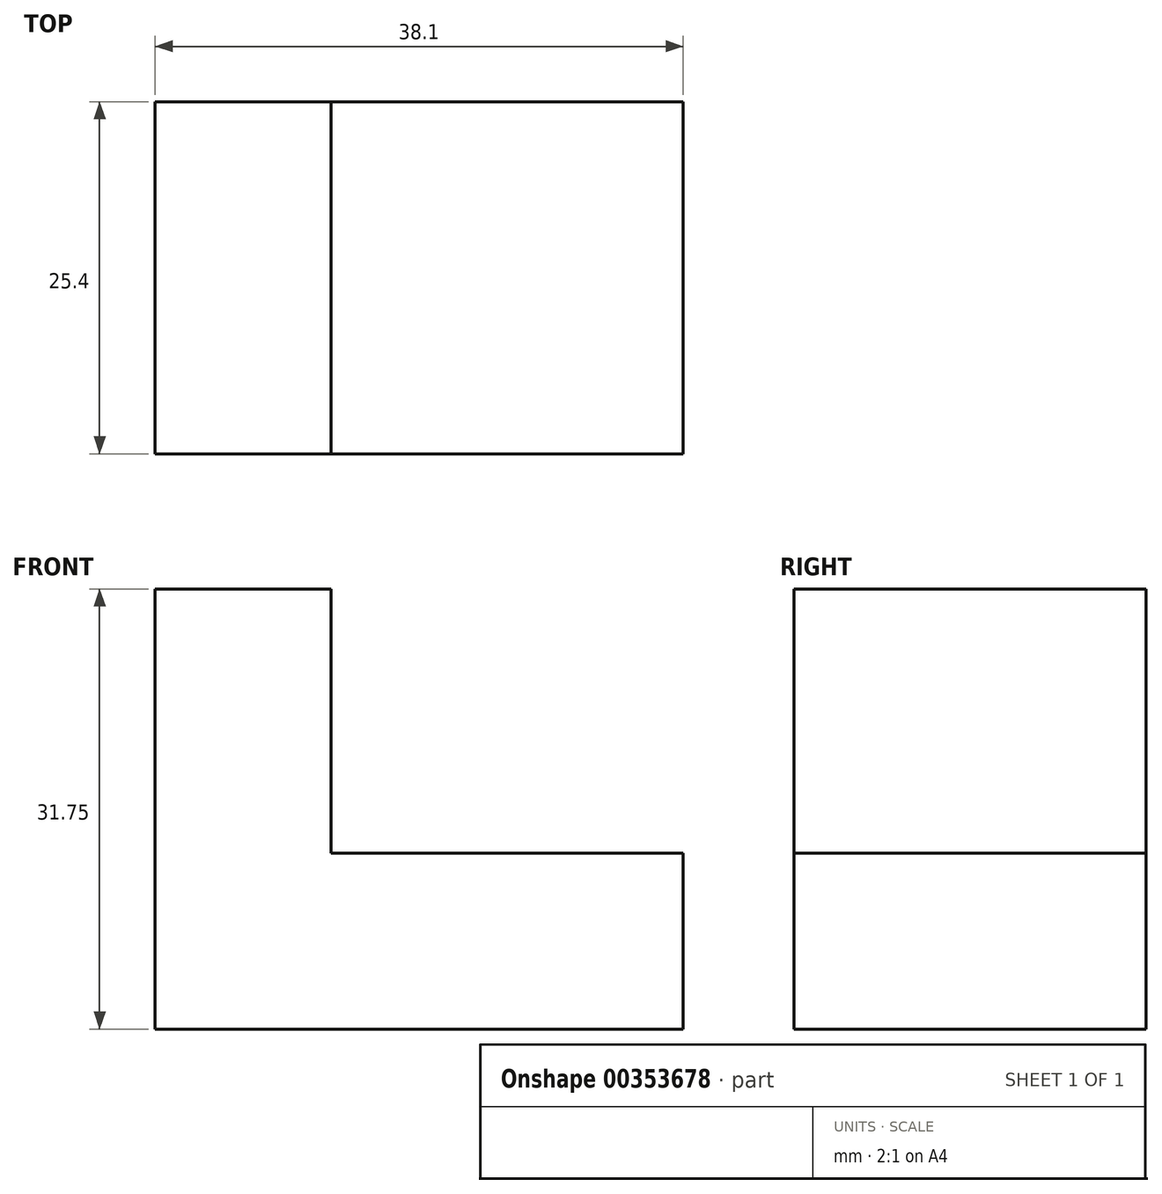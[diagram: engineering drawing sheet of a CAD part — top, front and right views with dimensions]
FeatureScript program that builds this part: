
annotation { "Feature Type Name" : "Feature", "Feature Type Description" : "" }
export const myFeature = defineFeature(function(context is Context, id is Id, definition is map)
    precondition{}
    {
        {
            var Q0;
            Q0=qCreatedBy(makeId("Front.planeOp"),FACE);
            var sketch = newSketch(context, id + "F0", { "sketchPlane" : qUnion([Q0])});
            skLineSegment(sketch, "E0", {"start": v(12.1, 31.75) * mm, "end": v(12.1, 0) * mm});
            skLineSegment(sketch, "E1", {"start": v(12.1, 0) * mm, "end": v(50.2, 0) * mm});
            skLineSegment(sketch, "E2", {"start": v(50.2, 0) * mm, "end": v(50.2, 12.7) * mm});
            skLineSegment(sketch, "E3", {"start": v(50.2, 12.7) * mm, "end": v(24.8, 12.7) * mm});
            skLineSegment(sketch, "E4", {"start": v(24.8, 12.7) * mm, "end": v(24.8, 31.75) * mm});
            skLineSegment(sketch, "E5", {"start": v(24.8, 31.75) * mm, "end": v(12.1, 31.75) * mm});
            skSolve(sketch);
        }
        {
            var Q0;
            Q0=makeQuery(id+"F0.imprint","IMPRINT",FACE,{"disambiguationData":[TD([[makeQuery(id+"F0.imprint","IMPRINT",EDGE,{"derivedFrom":sQuery(id+"F0.wireOp",EDGE,"E0")}),1.0]])]});
            extrude(context, id + "F1", {"entities" : qUnion([Q0]), "depth" : 25.4 * mm});
        }
    });
